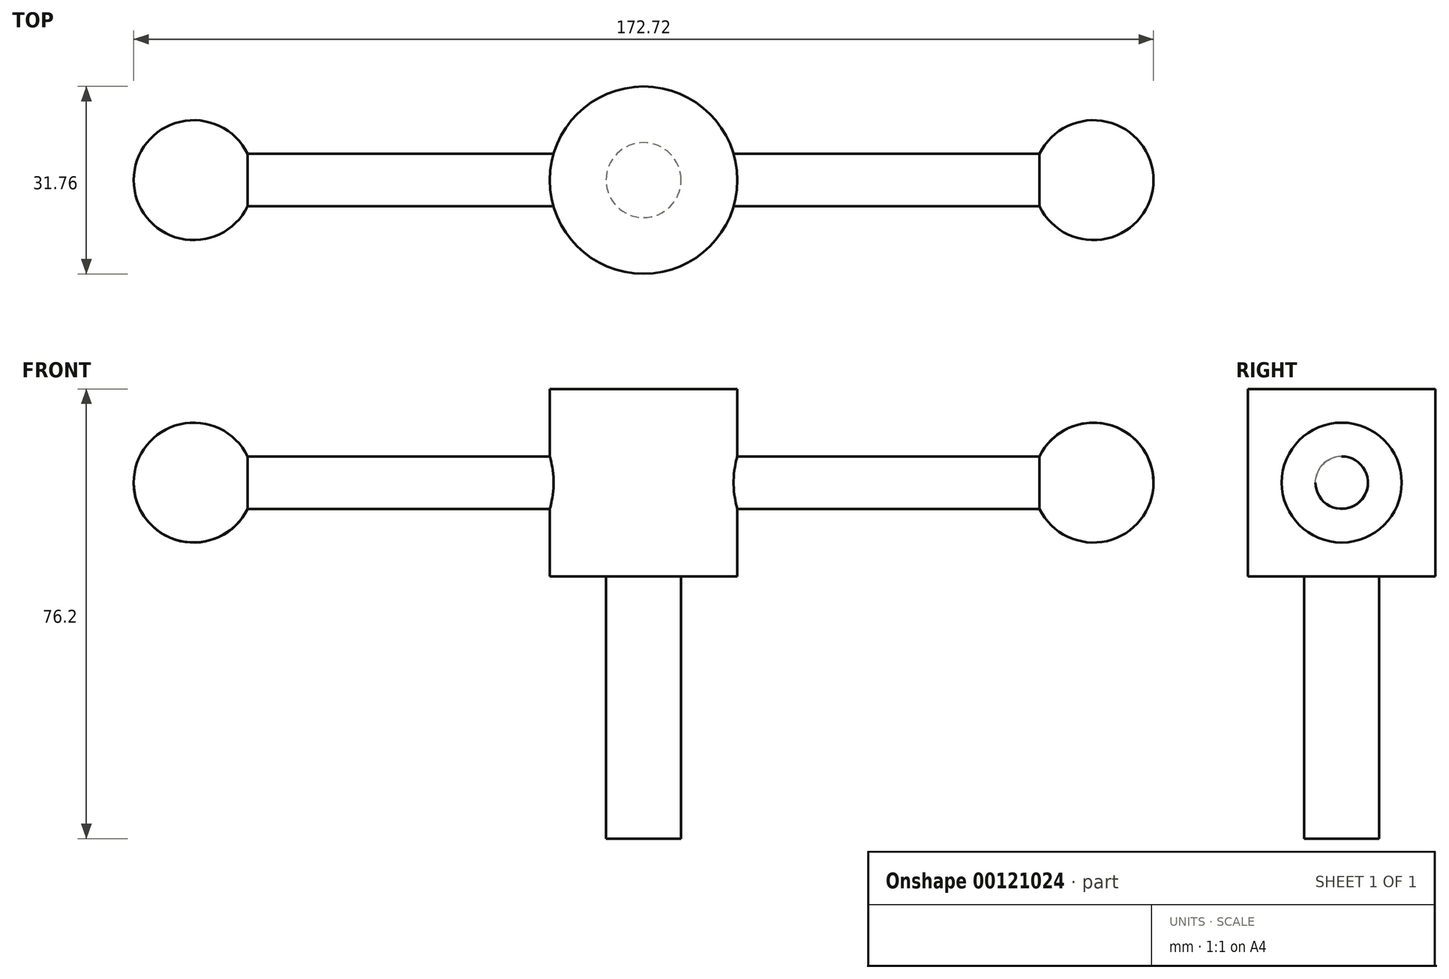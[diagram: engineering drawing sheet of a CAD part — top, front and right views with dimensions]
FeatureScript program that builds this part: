
annotation { "Feature Type Name" : "Feature", "Feature Type Description" : "" }
export const myFeature = defineFeature(function(context is Context, id is Id, definition is map)
    precondition{}
    {
        {
            var Q0;
            Q0=qCreatedBy(makeId("Top.planeOp"),FACE);
            var sketch = newSketch(context, id + "F0", { "sketchPlane" : qUnion([Q0])});
            skCircle(sketch, "E0", {"center": v(0, 0) * mm, "radius": 15.88 * mm});
            skCircle(sketch, "E1", {"center": v(0, 0) * mm, "radius": 6.35 * mm});
            skSolve(sketch);
        }
        {
            var Q0;
            Q0=makeQuery(id+"F0.imprint","IMPRINT",FACE,{"disambiguationData":[TD([[makeQuery(id+"F0.imprint","IMPRINT",EDGE,{"derivedFrom":sQuery(id+"F0.wireOp",EDGE,"E0")}),1.0]])]});
            var Q1;
            Q1=makeQuery(id+"F0.imprint","IMPRINT",FACE,{"disambiguationData":[TD([[makeQuery(id+"F0.imprint","IMPRINT",EDGE,{"derivedFrom":sQuery(id+"F0.wireOp",EDGE,"E1")}),1.0]])]});
            extrude(context, id + "F1", {"entities" : qUnion([Q0, Q1]), "depth" : 31.75 * mm});
        }
        {
            var Q0;
            Q0=makeQuery(id+"F0.imprint","IMPRINT",FACE,{"disambiguationData":[TD([[makeQuery(id+"F0.imprint","IMPRINT",EDGE,{"derivedFrom":sQuery(id+"F0.wireOp",EDGE,"E1")}),1.0]])]});
            extrude(context, id + "F2", {"entities" : qUnion([Q0]), "operationType" : NewBodyOperationType.ADD, "oppositeDirection" : true, "depth" : 44.45 * mm});
        }
        {
            var Q0;
            Q0=qCreatedBy(makeId("Right.planeOp"),FACE);
            var sketch = newSketch(context, id + "F3", { "sketchPlane" : qUnion([Q0])});
            skCircle(sketch, "E2", {"center": v(0, 15.88) * mm, "radius": 4.45 * mm});
            skSolve(sketch);
        }
        {
            var Q0;
            Q0 = qSketchRegion(id + "F3", true);
            extrude(context, id + "F4", {"entities" : qUnion([Q0]), "operationType" : NewBodyOperationType.ADD, "oppositeDirection" : true, "depth" : 76.2 * mm, "hasSecondDirection" : true, "secondDirectionOppositeDirection" : false, "secondDirectionDepth" : 76.2 * mm});
        }
        {
            var Q0;
            Q0=qCreatedBy(makeId("Front.planeOp"),FACE);
            var sketch = newSketch(context, id + "F5", { "sketchPlane" : qUnion([Q0])});
            skLineSegment(sketch, "E3", {"start": v(0, 50.12) * mm, "end": v(0, -71.95) * mm, "construction": true});
            skLineSegment(sketch, "E4.0", {"start": v(76.2, 20.32) * mm, "end": v(76.2, 11.43) * mm});
            skLineSegment(sketch, "E5", {"start": v(76.2, 15.88) * mm, "end": v(-89.61, 15.88) * mm, "construction": true});
            skLineSegment(sketch, "E6", {"start": v(66.04, 15.88) * mm, "end": v(86.36, 15.88) * mm});
            skArc(sketch, "E7", {"start": v(86.36, 15.88) * mm, "mid": v(76.2, 26.04) * mm, "end": v(66.04, 15.87) * mm});
            skCircle(sketch, "E8", {"center": v(76.2, 15.88) * mm, "radius": 10.16 * mm, "construction": true});
            skLineSegment(sketch, "E9.0", {"start": v(-76.2, 20.32) * mm, "end": v(-76.2, 11.43) * mm});
            skCircle(sketch, "E10", {"center": v(-76.2, 15.88) * mm, "radius": 10.16 * mm, "construction": true});
            skLineSegment(sketch, "E11", {"start": v(-66.04, 15.88) * mm, "end": v(-86.36, 15.88) * mm});
            skArc(sketch, "E12", {"start": v(-66.04, 15.88) * mm, "mid": v(-76.2, 26.03) * mm, "end": v(-86.36, 15.88) * mm});
            skSolve(sketch);
        }
        {
            var Q0;
            {var subQ0=sQuery(id+"F5.wireOp",EDGE,"E12");Q0=makeQuery(id+"F5.imprint","IMPRINT",FACE,{"disambiguationData":[TD([[makeQuery(id+"F5.imprint","IMPRINT",EDGE,{"derivedFrom":subQ0}),1.0]])]});}
            var Q1;
            Q1=sQuery(id+"F5.wireOp",EDGE,"E11");
            revolve(context, id + "F6", {"operationType" : NewBodyOperationType.ADD, "entities" : qUnion([Q0]), "axis" : qUnion([Q1]), "revolveType" : RevolveType.FULL});
        }
        {
            var Q0;
            {var subQ0=sQuery(id+"F5.wireOp",EDGE,"E7");Q0=makeQuery(id+"F5.imprint","IMPRINT",FACE,{"disambiguationData":[TD([[makeQuery(id+"F5.imprint","IMPRINT",EDGE,{"derivedFrom":subQ0}),1.0]])]});}
            var Q1;
            Q1=sQuery(id+"F5.wireOp",EDGE,"E6");
            revolve(context, id + "F7", {"operationType" : NewBodyOperationType.ADD, "entities" : qUnion([Q0]), "axis" : qUnion([Q1]), "revolveType" : RevolveType.FULL});
        }
    });
